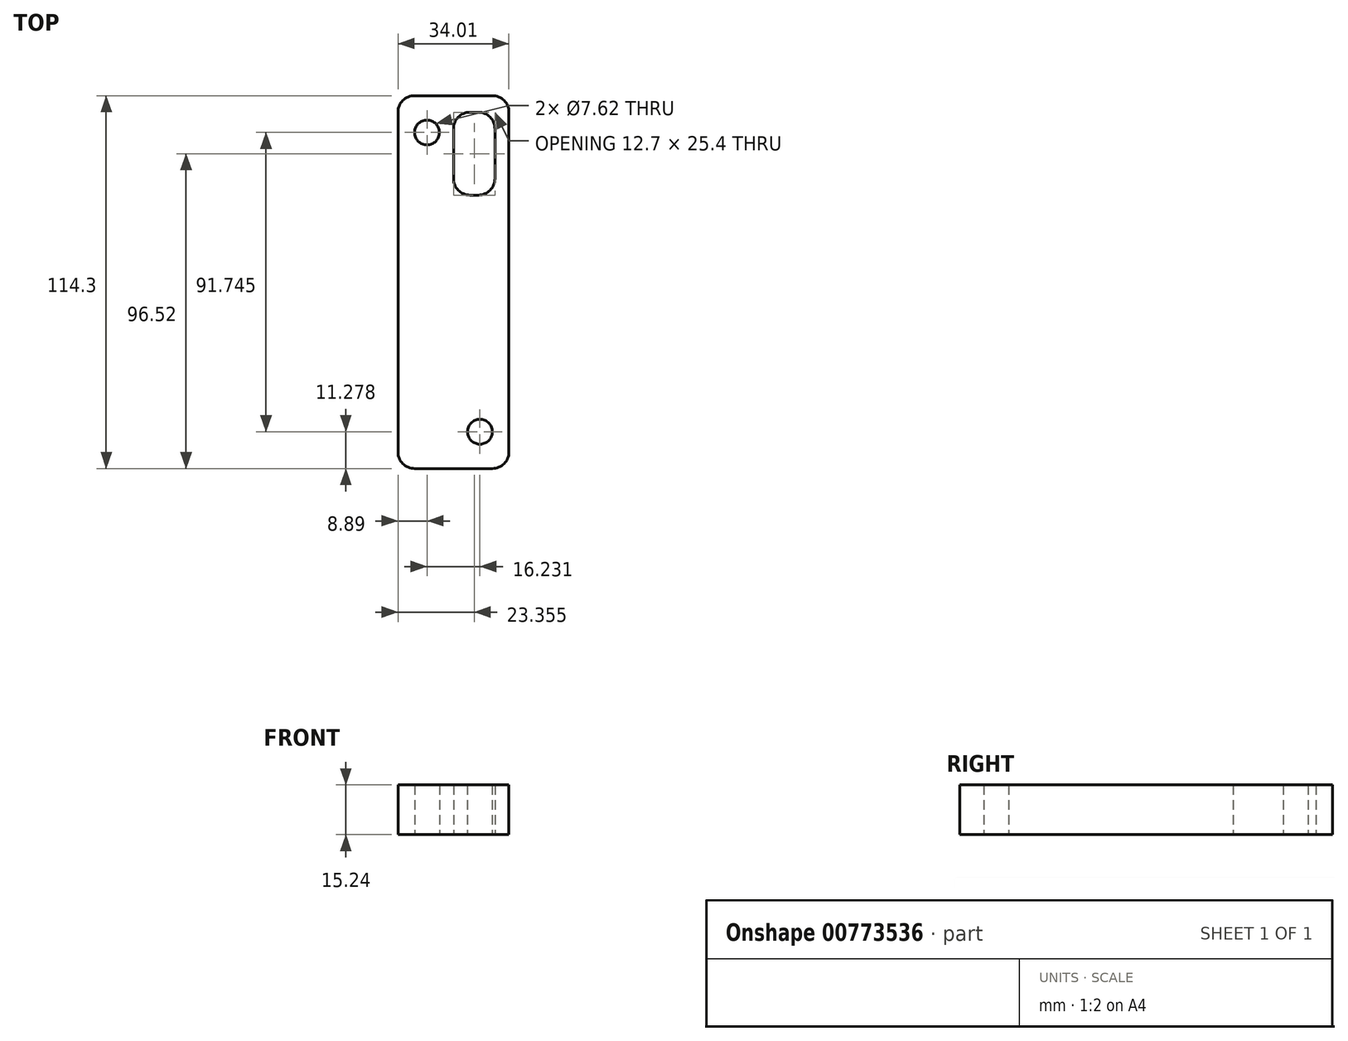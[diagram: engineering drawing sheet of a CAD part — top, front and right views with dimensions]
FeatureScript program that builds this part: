
annotation { "Feature Type Name" : "Feature", "Feature Type Description" : "" }
export const myFeature = defineFeature(function(context is Context, id is Id, definition is map)
    precondition{}
    {
        {
            var Q0;
            Q0=qCreatedBy(makeId("Top.planeOp"),FACE);
            var sketch = newSketch(context, id + "F0", { "sketchPlane" : qUnion([Q0])});
            skLineSegment(sketch, "E0.bottom", {"start": v(5.08, 0) * mm, "end": v(28.93, 0) * mm});
            skLineSegment(sketch, "E0.top", {"start": v(5.08, 114.3) * mm, "end": v(28.93, 114.3) * mm});
            skLineSegment(sketch, "E0.left", {"start": v(0, 5.08) * mm, "end": v(0, 109.22) * mm});
            skLineSegment(sketch, "E0.right", {"start": v(34.01, 5.08) * mm, "end": v(34.01, 109.22) * mm});
            skCircle(sketch, "E1", {"center": v(8.89, 103.02) * mm, "radius": 3.81 * mm});
            skCircle(sketch, "E2", {"center": v(25.12, 11.28) * mm, "radius": 3.81 * mm});
            skLineSegment(sketch, "E3.bottom", {"start": v(22.09, 109.22) * mm, "end": v(24.63, 109.22) * mm});
            skLineSegment(sketch, "E3.top", {"start": v(22.09, 83.82) * mm, "end": v(24.63, 83.82) * mm});
            skLineSegment(sketch, "E3.left", {"start": v(17, 104.14) * mm, "end": v(17, 88.9) * mm});
            skLineSegment(sketch, "E3.right", {"start": v(29.7, 104.14) * mm, "end": v(29.7, 88.9) * mm});
            skPoint(sketch, "E4.visualSharp", {"position": v(0, 114.3) * mm});
            skArc(sketch, "E4.filletArc", {"start": v(5.08, 114.3) * mm, "mid": v(1.49, 112.81) * mm, "end": v(0, 109.22) * mm});
            skPoint(sketch, "E5.visualSharp", {"position": v(34.01, 114.3) * mm});
            skArc(sketch, "E5.filletArc", {"start": v(34.01, 109.22) * mm, "mid": v(32.52, 112.81) * mm, "end": v(28.93, 114.3) * mm});
            skPoint(sketch, "E6.visualSharp", {"position": v(0, 0) * mm});
            skArc(sketch, "E6.filletArc", {"start": v(0, 5.08) * mm, "mid": v(1.49, 1.49) * mm, "end": v(5.08, 0) * mm});
            skPoint(sketch, "E7.visualSharp", {"position": v(34.01, 0) * mm});
            skArc(sketch, "E7.filletArc", {"start": v(28.93, 0) * mm, "mid": v(32.52, 1.49) * mm, "end": v(34.01, 5.08) * mm});
            skPoint(sketch, "E8.visualSharp", {"position": v(17, 83.82) * mm});
            skArc(sketch, "E8.filletArc", {"start": v(17, 88.9) * mm, "mid": v(18.5, 85.3) * mm, "end": v(22.09, 83.82) * mm});
            skPoint(sketch, "E9.visualSharp", {"position": v(17, 109.22) * mm});
            skArc(sketch, "E9.filletArc", {"start": v(22.09, 109.22) * mm, "mid": v(18.5, 107.73) * mm, "end": v(17, 104.14) * mm});
            skPoint(sketch, "E10.visualSharp", {"position": v(29.7, 109.22) * mm});
            skArc(sketch, "E10.filletArc", {"start": v(29.7, 104.14) * mm, "mid": v(28.22, 107.73) * mm, "end": v(24.63, 109.22) * mm});
            skPoint(sketch, "E11.visualSharp", {"position": v(29.7, 83.82) * mm});
            skArc(sketch, "E11.filletArc", {"start": v(24.63, 83.82) * mm, "mid": v(28.22, 85.3) * mm, "end": v(29.7, 88.9) * mm});
            skSolve(sketch);
        }
        {
            var Q0;
            Q0=makeQuery(id+"F0.imprint","IMPRINT",FACE,{"disambiguationData":[TD([[makeQuery(id+"F0.imprint","IMPRINT",EDGE,{"derivedFrom":sQuery(id+"F0.wireOp",EDGE,"E0.bottom")}),1.0]])]});
            extrude(context, id + "F1", {"entities" : qUnion([Q0]), "depth" : 15.24 * mm, "offsetDistance" : 25.4 * mm});
        }
    });
